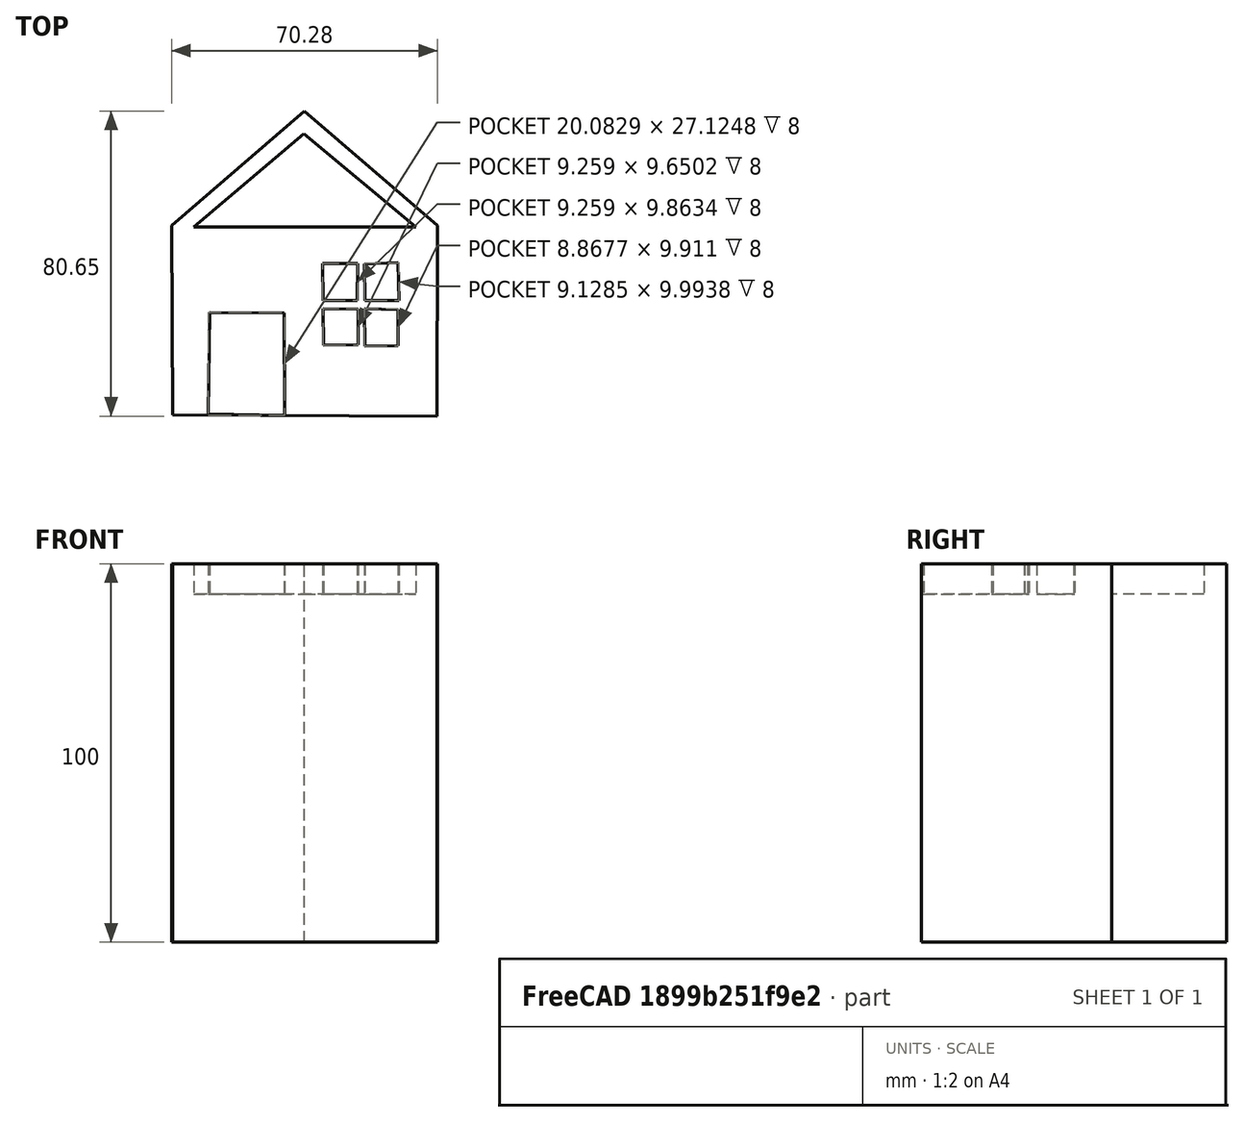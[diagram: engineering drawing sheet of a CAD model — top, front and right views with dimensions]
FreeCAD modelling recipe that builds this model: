
FCSTD DOCUMENT  (FreeCAD 0.21R33771 (Git))
Label: OJT1_T17R02_caseta
License: All rights reserved
LicenseURL: http://en.wikipedia.org/wiki/All_rights_reserved
objects: Sketcher::SketchObject×3, PartDesign::Pocket×2, PartDesign::Pad×1, PartDesign::Body×1
note: 10 computed .brp shape members not serialized (recipe doc carries the construction recipe); baked Part::Feature solids carry a one-line shape summary decoded from their .brp

FEATURE [Sketcher::SketchObject] Sketch
  FullyConstrained = false
  MapMode = 5
  Support = -> [XY_Plane]
  sketch-geometry (5):
    g0: LineSegment StartX=-79.5623 StartY=-30.2216 StartZ=0 EndX=-9.79176 EndY=-30.5562 EndZ=0
    g1: LineSegment StartX=-9.79176 StartY=-30.5562 StartZ=0 EndX=-9.62445 EndY=19.8057 EndZ=0
    g2: LineSegment StartX=-9.62445 StartY=19.8057 StartZ=0 EndX=-44.7607 EndY=50.0898 EndZ=0
    g3: LineSegment StartX=-44.7607 StartY=50.0898 StartZ=0 EndX=-79.8969 EndY=19.8057 EndZ=0
    g4: LineSegment StartX=-79.8969 StartY=19.8057 StartZ=0 EndX=-79.5623 EndY=-30.2216 EndZ=0
  constraints (5):
    c: Coincident(g0,g1)
    c: Coincident(g1,g2)
    c: Coincident(g2,g3)
    c: Coincident(g3,g4)
    c: Coincident(g4,g0)
FEATURE [PartDesign::Pad] Pad
  Direction = (0,0,1)
  Length = 100
  Length2 = 10
  Profile = -> Sketch
  ReferenceAxis = -> Sketch [N_Axis]
  Type = 0
FEATURE [Sketcher::SketchObject] Sketch001
  FullyConstrained = false
  MapMode = 5
  Placement = pos=(0,0,100) rot=(0,0,1;0rad)
  Support = -> [Pad]
  sketch-geometry (3):
    g0: LineSegment StartX=-74.0553 StartY=19.4605 StartZ=0 EndX=-44.9069 EndY=44.1491 EndZ=0
    g1: LineSegment StartX=-44.9069 StartY=44.1491 StartZ=0 EndX=-15.2807 EndY=19.4605 EndZ=0
    g2: LineSegment StartX=-15.2807 StartY=19.4605 StartZ=0 EndX=-74.0553 EndY=19.4605 EndZ=0
  constraints (4):
    c: Coincident(g0,g1)
    c: Coincident(g1,g2)
    c: Coincident(g2,g0)
    c: Horizontal(g2)
FEATURE [PartDesign::Pocket] Pocket
  BaseFeature = -> Pad
  Direction = (0,0,-1)
  Length = 8
  Length2 = 5
  Profile = -> Sketch001
  ReferenceAxis = -> Sketch001 [N_Axis]
  Type = 0
FEATURE [Sketcher::SketchObject] Sketch002
  FullyConstrained = false
  MapMode = 5
  Placement = pos=(0,0,100) rot=(0,0,1;0rad)
  Support = -> [Pocket]
  sketch-geometry (20):
    g0: LineSegment StartX=-70.1489 StartY=-29.9111 StartZ=0 EndX=-69.8881 EndY=-3.17746 EndZ=0
    g1: LineSegment StartX=-69.8881 StartY=-3.17746 StartZ=0 EndX=-50.1965 EndY=-3.30787 EndZ=0
    g2: LineSegment StartX=-50.1965 StartY=-3.30787 StartZ=0 EndX=-50.066 EndY=-30.3023 EndZ=0
    g3: LineSegment StartX=-50.066 StartY=-30.3023 StartZ=0 EndX=-70.1489 EndY=-29.9111 EndZ=0
    g4: LineSegment StartX=-40.0246 StartY=9.86335 StartZ=0 EndX=-39.8942 EndY=0 EndZ=0
    g5: LineSegment StartX=-39.8942 StartY=0 StartZ=0 EndX=-30.896 EndY=0 EndZ=0
    g6: LineSegment StartX=-30.896 StartY=0 StartZ=0 EndX=-30.7656 EndY=9.86335 EndZ=0
    g7: LineSegment StartX=-30.7656 StartY=9.86335 StartZ=0 EndX=-40.0246 EndY=9.86335 EndZ=0
    g8: LineSegment StartX=-28.9399 StartY=9.73294 StartZ=0 EndX=-20.0722 EndY=9.99376 EndZ=0
    g9: LineSegment StartX=-20.0722 StartY=9.99376 StartZ=0 EndX=-19.8114 EndY=0 EndZ=0
    g10: LineSegment StartX=-19.8114 StartY=0 StartZ=0 EndX=-28.8095 EndY=0 EndZ=0
    g11: LineSegment StartX=-28.8095 StartY=0 StartZ=0 EndX=-28.9399 EndY=9.73294 EndZ=0
    g12: LineSegment StartX=-39.8942 StartY=-2.13419 StartZ=0 EndX=-30.6352 EndY=-2.2646 EndZ=0
    g13: LineSegment StartX=-30.6352 StartY=-2.2646 StartZ=0 EndX=-30.6352 EndY=-11.654 EndZ=0
    g14: LineSegment StartX=-30.6352 StartY=-11.654 StartZ=0 EndX=-39.7638 EndY=-11.7844 EndZ=0
    g15: LineSegment StartX=-39.7638 StartY=-11.7844 StartZ=0 EndX=-39.8942 EndY=-2.13419 EndZ=0
    g16: LineSegment StartX=-28.9399 StartY=-2.13419 StartZ=0 EndX=-20.0722 EndY=-2.39501 EndZ=0
    g17: LineSegment StartX=-20.0722 StartY=-2.39501 StartZ=0 EndX=-20.0722 EndY=-11.9148 EndZ=0
    g18: LineSegment StartX=-20.0722 StartY=-11.9148 StartZ=0 EndX=-28.8095 EndY=-12.0452 EndZ=0
    g19: LineSegment StartX=-28.8095 StartY=-12.0452 StartZ=0 EndX=-28.9399 EndY=-2.13419 EndZ=0
  constraints (19):
    c: Coincident(g0,g1)
    c: Coincident(g1,g2)
    c: Coincident(g2,g3)
    c: Coincident(g3,g0)
    c: Coincident(g4,g5)
    c: Coincident(g5,g6)
    c: Coincident(g6,g7)
    c: Coincident(g7,g4)
    c: Coincident(g8,g9)
    c: Coincident(g9,g10)
    c: Coincident(g10,g11)
    c: Coincident(g11,g8)
    c: Coincident(g12,g13)
    c: Coincident(g13,g14)
    c: Coincident(g14,g15)
    c: Coincident(g15,g12)
    c: Coincident(g16,g17)
    c: Coincident(g17,g18)
    c: Coincident(g18,g19)
FEATURE [PartDesign::Pocket] Pocket001  label="caseta"
  BaseFeature = -> Pocket
  Direction = (0,0,-1)
  Length = 8
  Length2 = 5
  Profile = -> Sketch002
  ReferenceAxis = -> Sketch002 [N_Axis]
  Type = 0
FEATURE [PartDesign::Body] Body
  Group = -> [Sketch,Pad,Sketch001,Pocket,Sketch002,Pocket001]
  Origin = -> Origin
  Tip = -> Pocket001
